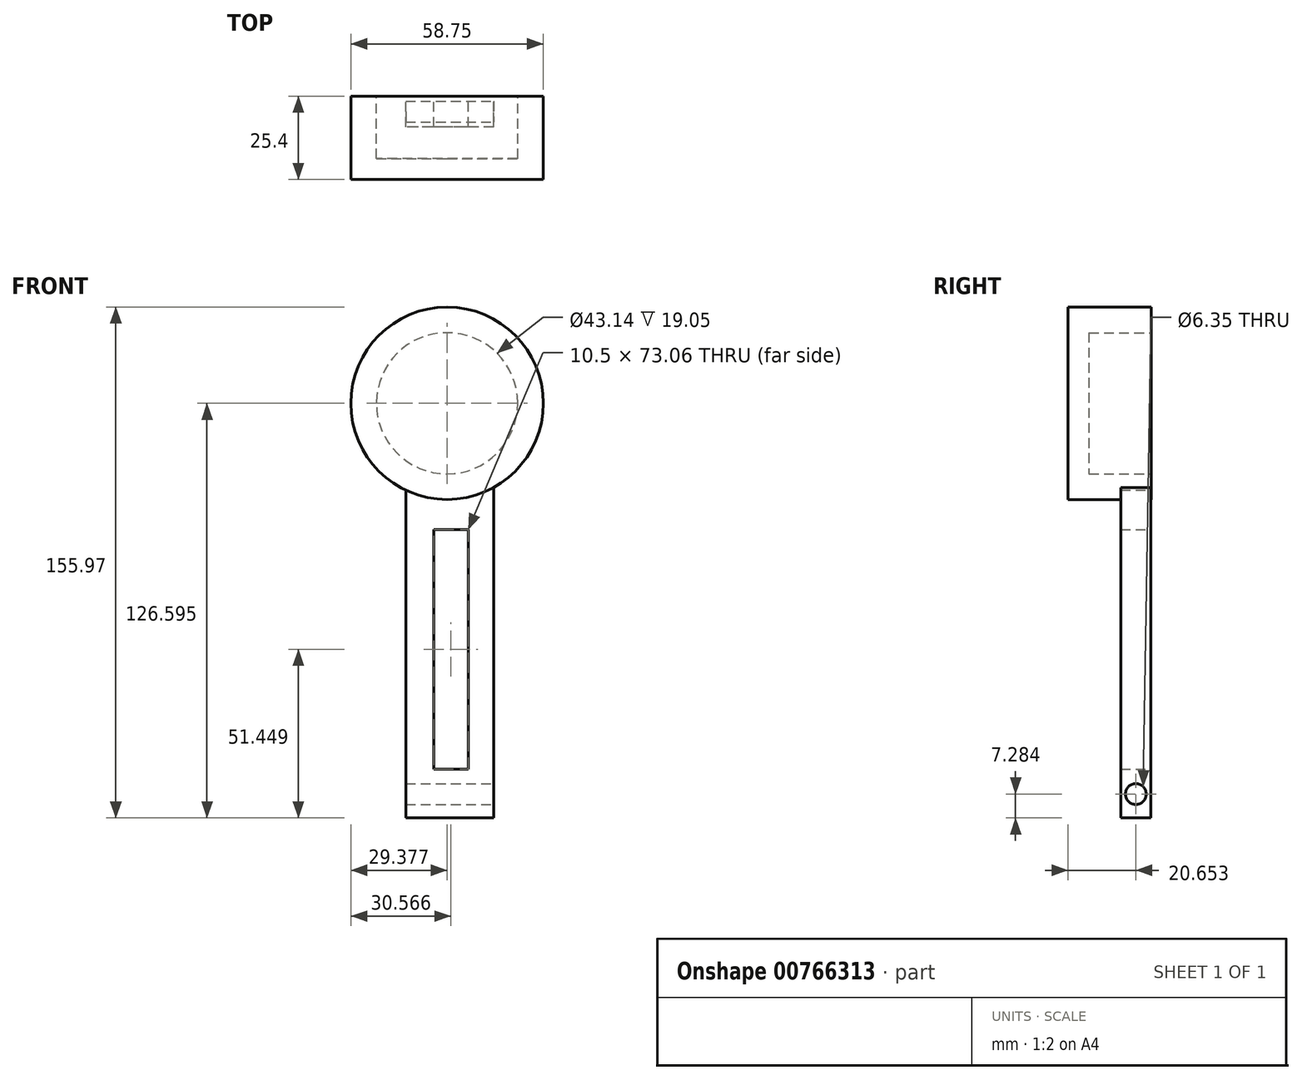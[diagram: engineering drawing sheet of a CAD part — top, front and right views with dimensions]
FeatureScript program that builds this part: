
annotation { "Feature Type Name" : "Feature", "Feature Type Description" : "" }
export const myFeature = defineFeature(function(context is Context, id is Id, definition is map)
    precondition{}
    {
        {
            var Q0;
            Q0=qCreatedBy(makeId("Front.planeOp"),FACE);
            var sketch = newSketch(context, id + "F0", { "sketchPlane" : qUnion([Q0])});
            skCircle(sketch, "E0", {"center": v(-56.84, 24.07) * mm, "radius": 29.38 * mm});
            skCircle(sketch, "E1", {"center": v(-56.84, 24.07) * mm, "radius": 20.46 * mm});
            skSolve(sketch);
        }
        {
            var Q0;
            Q0=makeQuery(id+"F0.imprint","IMPRINT",FACE,{"disambiguationData":[TD([[makeQuery(id+"F0.imprint","IMPRINT",EDGE,{"derivedFrom":sQuery(id+"F0.wireOp",EDGE,"E0")}),1.0]])]});
            var Q1;
            Q1=makeQuery(id+"F0.imprint","IMPRINT",FACE,{"disambiguationData":[TD([[makeQuery(id+"F0.imprint","IMPRINT",EDGE,{"derivedFrom":sQuery(id+"F0.wireOp",EDGE,"E1")}),1.0]])]});
            extrude(context, id + "F1", {"entities" : qUnion([Q0, Q1]), "depth" : 25.4 * mm, "offsetDistance" : 25.4 * mm});
        }
        {
            var Q0;
            Q0=makeQuery(id+"F1.opExtrude","CAP_FACE",FACE,{"disambiguationData":[OSD([sQuery(id+"F0.wireOp",EDGE,"E0")])],"isStart":true});
            var sketch = newSketch(context, id + "F2", { "sketchPlane" : qUnion([Q0])});
            skCircle(sketch, "E2", {"center": v(56.84, 24.07) * mm, "radius": 21.57 * mm});
            skSolve(sketch);
        }
        {
            var Q0;
            Q0=qCreatedBy(makeId("Top.planeOp"),FACE);
            var sketch = newSketch(context, id + "F3", { "sketchPlane" : qUnion([Q0])});
            skLineSegment(sketch, "E3.bottom", {"start": v(-42.64, -0.11) * mm, "end": v(-69.46, -0.11) * mm});
            skLineSegment(sketch, "E3.top", {"start": v(-42.64, -9.37) * mm, "end": v(-69.46, -9.37) * mm});
            skLineSegment(sketch, "E3.left", {"start": v(-42.64, -0.11) * mm, "end": v(-42.64, -9.37) * mm});
            skLineSegment(sketch, "E3.right", {"start": v(-69.46, -0.11) * mm, "end": v(-69.46, -9.37) * mm});
            skSolve(sketch);
        }
        {
            var Q0;
            Q0 = qSketchRegion(id + "F3", true);
            extrude(context, id + "F4", {"entities" : qUnion([Q0]), "operationType" : NewBodyOperationType.ADD, "oppositeDirection" : true, "depth" : 102.53 * mm, "offsetDistance" : 25.4 * mm});
        }
        {
            var Q0;
            Q0=makeQuery(id+"F2.imprint","IMPRINT",FACE,{"disambiguationData":[TD([[makeQuery(id+"F2.imprint","IMPRINT",EDGE,{"derivedFrom":sQuery(id+"F2.wireOp",EDGE,"E2")}),1.0]])]});
            extrude(context, id + "F5", {"entities" : qUnion([Q0]), "operationType" : NewBodyOperationType.REMOVE, "oppositeDirection" : true, "depth" : 19.05 * mm, "offsetDistance" : 25.4 * mm});
        }
        {
            var Q0;
            Q0=makeQuery(id+"F4.opExtrude","SWEPT_FACE",FACE,{"disambiguationData":[OSD([sQuery(id+"F3.wireOp",EDGE,"E3.left")])]});
            var sketch = newSketch(context, id + "F6", { "sketchPlane" : qUnion([Q0])});
            skSolve(sketch);
        }
        {
            var Q0;
            {var subQ0=sQuery(id+"F3.wireOp",EDGE,"E3.left");Q0=makeQuery(id+"F6.imprint","IMPRINT",FACE,{"disambiguationData":[TD([[makeQuery(id+"F6.imprint","IMPRINT",EDGE,{"derivedFrom":makeQuery(id+"F4.opExtrude","CAP_EDGE",EDGE,{"disambiguationData":[OSD([subQ0])],"isStart":false})}),-1.0]])]});}
            var sketch = newSketch(context, id + "F7", { "sketchPlane" : qUnion([Q0])});
            skCircle(sketch, "E4", {"center": v(-4.75, -95.25) * mm, "radius": 3.18 * mm});
            skSolve(sketch);
        }
        {
            var Q0;
            Q0 = qSketchRegion(id + "F7", true);
            extrude(context, id + "F8", {"entities" : qUnion([Q0]), "operationType" : NewBodyOperationType.REMOVE, "oppositeDirection" : true, "depth" : 50.8 * mm, "offsetDistance" : 25.4 * mm});
        }
        {
            var Q0;
            Q0=makeQuery(id+"F4.opExtrude","SWEPT_FACE",FACE,{"disambiguationData":[OSD([sQuery(id+"F3.wireOp",EDGE,"E3.bottom")])]});
            var sketch = newSketch(context, id + "F9", { "sketchPlane" : qUnion([Q0])});
            skLineSegment(sketch, "E5.bottom", {"start": v(50.4, -14.55) * mm, "end": v(60.9, -14.55) * mm});
            skLineSegment(sketch, "E5.top", {"start": v(50.4, -87.61) * mm, "end": v(60.9, -87.61) * mm});
            skLineSegment(sketch, "E5.left", {"start": v(50.4, -14.55) * mm, "end": v(50.4, -87.61) * mm});
            skLineSegment(sketch, "E5.right", {"start": v(60.9, -14.55) * mm, "end": v(60.9, -87.61) * mm});
            skSolve(sketch);
        }
        {
            var Q0;
            Q0=makeQuery(id+"F9.imprint","IMPRINT",FACE,{"disambiguationData":[TD([[makeQuery(id+"F9.imprint","IMPRINT",EDGE,{"derivedFrom":sQuery(id+"F9.wireOp",EDGE,"E5.bottom")}),-1.0]])]});
            extrude(context, id + "F10", {"entities" : qUnion([Q0]), "operationType" : NewBodyOperationType.REMOVE, "oppositeDirection" : true, "depth" : 25.4 * mm, "offsetDistance" : 25.4 * mm});
        }
    });
